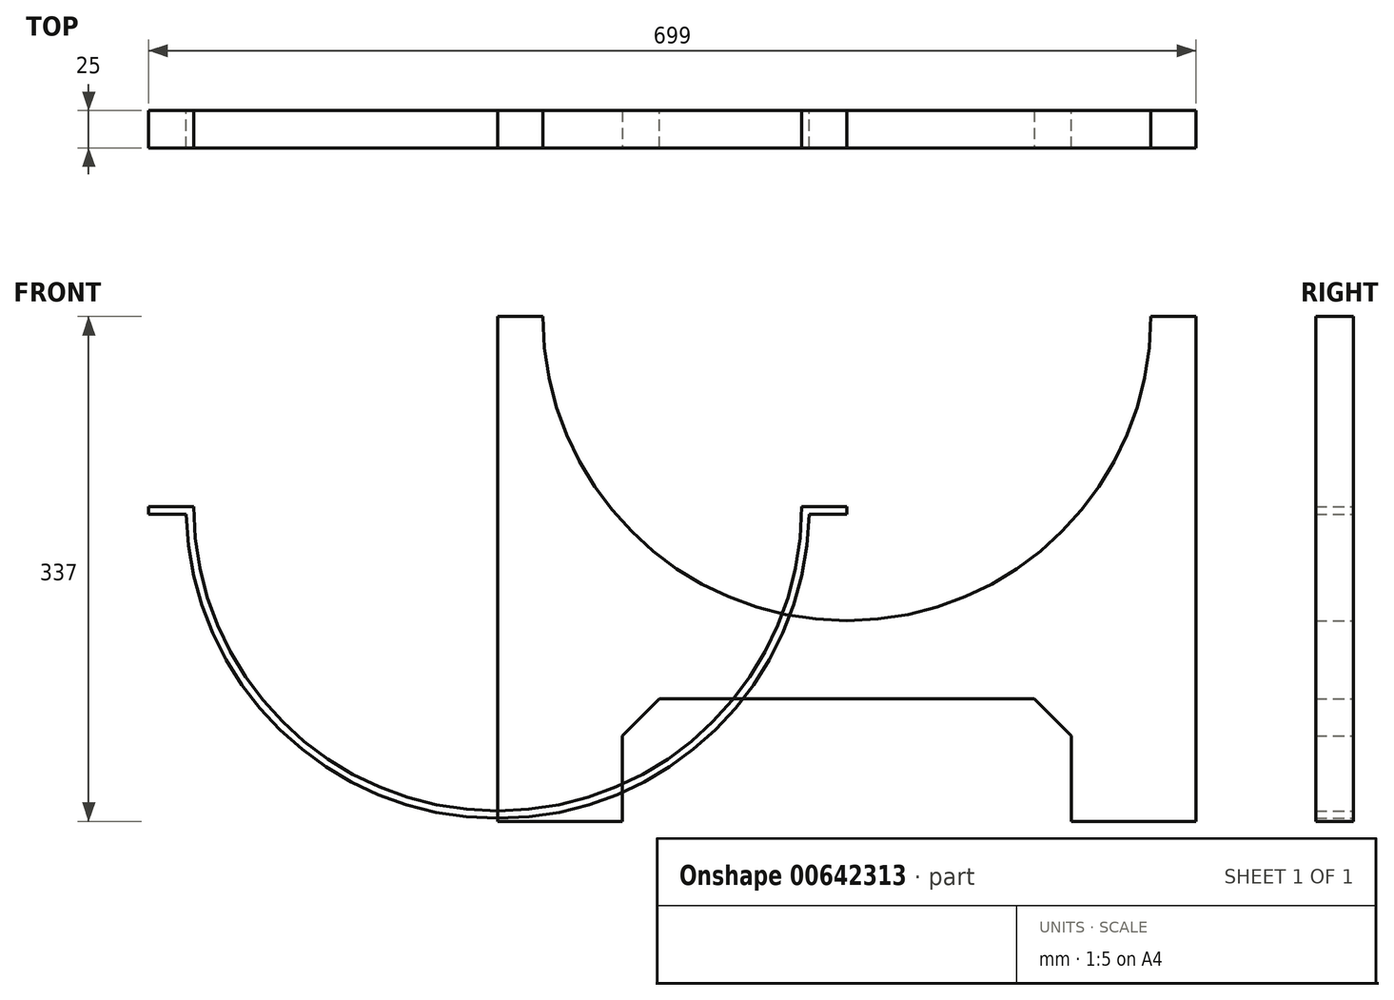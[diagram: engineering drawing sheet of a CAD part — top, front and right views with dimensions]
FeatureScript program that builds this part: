
annotation { "Feature Type Name" : "Feature", "Feature Type Description" : "" }
export const myFeature = defineFeature(function(context is Context, id is Id, definition is map)
    precondition{}
    {
        {
            var Q0;
            Q0=qCreatedBy(makeId("Front.planeOp"),FACE);
            var sketch = newSketch(context, id + "F0", { "sketchPlane" : qUnion([Q0])});
            skLineSegment(sketch, "E0", {"start": v(0, 0) * mm, "end": v(466, 0) * mm});
            skLineSegment(sketch, "E1", {"start": v(466, 0) * mm, "end": v(466, 330) * mm});
            skLineSegment(sketch, "E2", {"start": v(466, 330) * mm, "end": v(436, 330) * mm});
            skLineSegment(sketch, "E3", {"start": v(0, 0) * mm, "end": v(0, 330) * mm});
            skLineSegment(sketch, "E4", {"start": v(0, 330) * mm, "end": v(30, 330) * mm});
            skLineSegment(sketch, "E5", {"start": v(30, 330) * mm, "end": v(233, 330) * mm, "construction": true});
            skLineSegment(sketch, "E6", {"start": v(233, 330) * mm, "end": v(436, 330) * mm, "construction": true});
            skLineSegment(sketch, "E7", {"start": v(233, 330) * mm, "end": v(233, 127) * mm, "construction": true});
            skLineSegment(sketch, "E8", {"start": v(233, 127) * mm, "end": v(233, 0) * mm, "construction": true});
            skArc(sketch, "E9", {"start": v(30, 330) * mm, "mid": v(233, 127) * mm, "end": v(436, 330) * mm});
            skLineSegment(sketch, "E10.bottom", {"start": v(83, 0) * mm, "end": v(383, 0) * mm});
            skLineSegment(sketch, "E10.top", {"start": v(83, 75) * mm, "end": v(383, 75) * mm});
            skLineSegment(sketch, "E10.left", {"start": v(83, 0) * mm, "end": v(83, 75) * mm});
            skLineSegment(sketch, "E10.right", {"start": v(383, 0) * mm, "end": v(383, 75) * mm});
            skSolve(sketch);
        }
        {
            var Q0;
            {var subQ0=sQuery(id+"F0.wireOp",EDGE,"E1");Q0=makeQuery(id+"F0.imprint","IMPRINT",FACE,{"disambiguationData":[TD([[makeQuery(id+"F0.imprint","IMPRINT",EDGE,{"derivedFrom":subQ0}),1.0]])]});}
            extrude(context, id + "F1", {"entities" : qUnion([Q0]), "depth" : 25 * mm, "offsetDistance" : 25 * mm});
        }
        {
            var Q0;
            Q0=makeQuery(id+"F1.opExtrude","SWEPT_EDGE",EDGE,{"disambiguationData":[OSD([sQuery(id+"F0.wireOp",EDGE,"E10.top"),sQuery(id+"F0.wireOp",EDGE,"E10.left")])]});
            var Q1;
            Q1=makeQuery(id+"F1.opExtrude","SWEPT_EDGE",EDGE,{"disambiguationData":[OSD([sQuery(id+"F0.wireOp",EDGE,"E10.top"),sQuery(id+"F0.wireOp",EDGE,"E10.right")])]});
            chamfer(context, id + "F2", {"entities" : qUnion([Q0, Q1]), "width" : 25 * mm, "tangentPropagation" : true});
        }
        {
            var Q0;
            {var subQ0=sQuery(id+"F0.wireOp",EDGE,"E1");Q0=makeQuery(id+"F0.imprint","IMPRINT",FACE,{"disambiguationData":[TD([[makeQuery(id+"F0.imprint","IMPRINT",EDGE,{"derivedFrom":subQ0}),1.0]])]});}
            extrude(context, id + "F3", {"entities" : qUnion([Q0]), "depth" : 25 * mm, "offsetDistance" : 25 * mm});
        }
        {
            var Q0;
            Q0=makeQuery(id+"F3.opExtrude","SWEPT_EDGE",EDGE,{"disambiguationData":[OSD([sQuery(id+"F0.wireOp",EDGE,"E10.top"),sQuery(id+"F0.wireOp",EDGE,"E10.left")])]});
            var Q1;
            Q1=makeQuery(id+"F3.opExtrude","SWEPT_EDGE",EDGE,{"disambiguationData":[OSD([sQuery(id+"F0.wireOp",EDGE,"E10.top"),sQuery(id+"F0.wireOp",EDGE,"E10.right")])]});
            chamfer(context, id + "F4", {"entities" : qUnion([Q0, Q1]), "width" : 25 * mm, "tangentPropagation" : true});
        }
        {
            var Q0;
            {var subQ0=sQuery(id+"F0.wireOp",EDGE,"E0");Q0=makeQuery(id+"F3.opExtrude","SWEPT_FACE",FACE,{"disambiguationData":[OSD([subQ0]),TDD([makeQuery(id+"F0.imprint","IMPRINT",EDGE,{"disambiguationData":[TD([[makeQuery(id+"F0.imprint","INTERSECT",VERTEX,{"derivedFrom":[subQ0,sQuery(id+"F0.wireOp",EDGE,"E3")]}),-1.0]])],"derivedFrom":subQ0})])]});}
            var Q1;
            {var subQ0=sQuery(id+"F0.wireOp",EDGE,"E0");Q1=makeQuery(id+"F3.opExtrude","SWEPT_FACE",FACE,{"disambiguationData":[OSD([subQ0]),TDD([makeQuery(id+"F0.imprint","IMPRINT",EDGE,{"disambiguationData":[TD([[makeQuery(id+"F0.imprint","INTERSECT",VERTEX,{"derivedFrom":[subQ0,sQuery(id+"F0.wireOp",EDGE,"E1")]}),1.0]])],"derivedFrom":subQ0})])]});}
            extrude(context, id + "F5", {"entities" : qUnion([Q0, Q1]), "operationType" : NewBodyOperationType.ADD, "depth" : 7 * mm, "offsetDistance" : 25 * mm});
        }
        {
            var Q0;
            Q0=qCreatedBy(makeId("Front.planeOp"),FACE);
            var sketch = newSketch(context, id + "F6", { "sketchPlane" : qUnion([Q0])});
            skLineSegment(sketch, "E11", {"start": v(-233, -127) * mm, "end": v(233, -127) * mm});
            skLineSegment(sketch, "E12", {"start": v(233, -127) * mm, "end": v(233, 203) * mm});
            skLineSegment(sketch, "E13", {"start": v(233, 203) * mm, "end": v(203, 203) * mm});
            skLineSegment(sketch, "E14", {"start": v(-233, -127) * mm, "end": v(-233, 203) * mm});
            skLineSegment(sketch, "E15", {"start": v(-233, 203) * mm, "end": v(-203, 203) * mm});
            skLineSegment(sketch, "E16", {"start": v(-203, 203) * mm, "end": v(0, 203) * mm, "construction": true});
            skLineSegment(sketch, "E17", {"start": v(0, 203) * mm, "end": v(203, 203) * mm, "construction": true});
            skLineSegment(sketch, "E18", {"start": v(0, 203) * mm, "end": v(0, 0) * mm, "construction": true});
            skLineSegment(sketch, "E19", {"start": v(0, 0) * mm, "end": v(0, -127) * mm, "construction": true});
            skArc(sketch, "E20", {"start": v(-203, 203) * mm, "mid": v(0, 0) * mm, "end": v(203, 203) * mm});
            skLineSegment(sketch, "E21.bottom", {"start": v(-150, -127) * mm, "end": v(150, -127) * mm});
            skLineSegment(sketch, "E21.top", {"start": v(-150, -52) * mm, "end": v(150, -52) * mm});
            skLineSegment(sketch, "E21.left", {"start": v(-150, -127) * mm, "end": v(-150, -52) * mm});
            skLineSegment(sketch, "E21.right", {"start": v(150, -127) * mm, "end": v(150, -52) * mm});
            skLineSegment(sketch, "E22", {"start": v(-233, 198) * mm, "end": v(-208, 198) * mm});
            skLineSegment(sketch, "E23", {"start": v(233, 198) * mm, "end": v(208, 198) * mm});
            skArc(sketch, "E24", {"start": v(-208, 198) * mm, "mid": v(0, -5) * mm, "end": v(208, 198) * mm});
            skPoint(sketch, "E25", {"position": v(0, -5) * mm});
            skSolve(sketch);
        }
        {
            var Q0;
            {var subQ3=sQuery(id+"F6.wireOp",EDGE,"E13");Q0=makeQuery(id+"F6.imprint","IMPRINT",FACE,{"disambiguationData":[TD([[makeQuery(id+"F6.imprint","IMPRINT",EDGE,{"derivedFrom":subQ3}),1.0]])]});}
            extrude(context, id + "F7", {"entities" : qUnion([Q0]), "depth" : 25 * mm, "offsetDistance" : 25 * mm});
        }
    });
